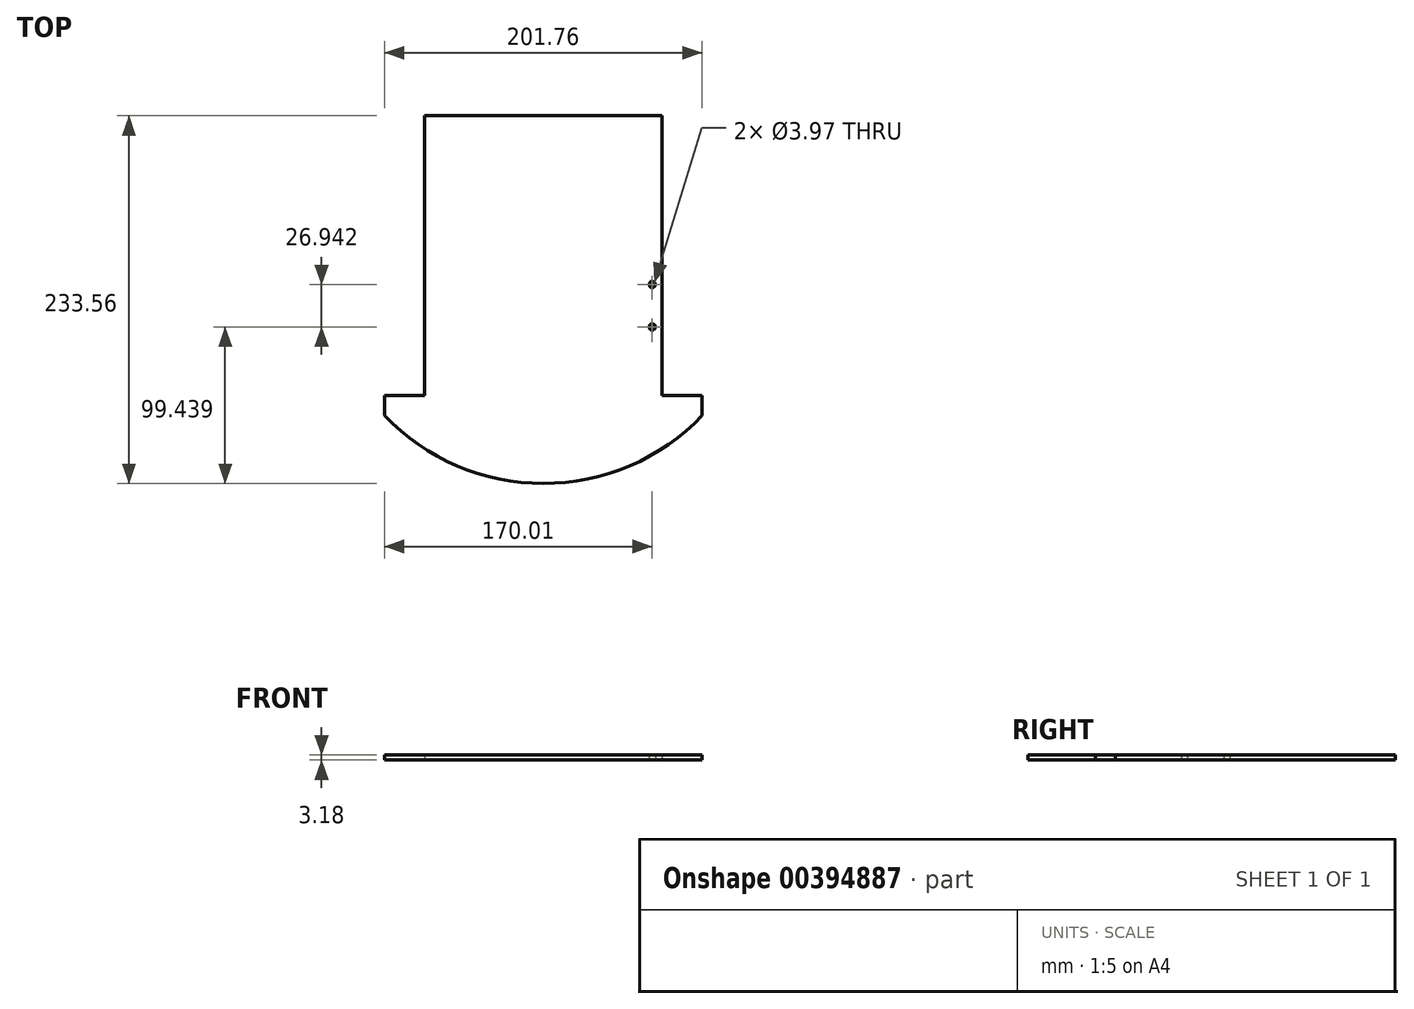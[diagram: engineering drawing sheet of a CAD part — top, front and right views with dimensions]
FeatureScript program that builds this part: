
annotation { "Feature Type Name" : "Feature", "Feature Type Description" : "" }
export const myFeature = defineFeature(function(context is Context, id is Id, definition is map)
    precondition{}
    {
        {
            var Q0;
            Q0=qCreatedBy(makeId("Top.planeOp"),FACE);
            var sketch = newSketch(context, id + "F0", { "sketchPlane" : qUnion([Q0])});
            skLineSegment(sketch, "E0.top", {"start": v(-75.48, 88.9) * mm, "end": v(75.48, 88.9) * mm});
            skLineSegment(sketch, "E0.left", {"start": v(-75.48, -88.9) * mm, "end": v(-75.48, 88.9) * mm});
            skLineSegment(sketch, "E0.right", {"start": v(75.48, -88.9) * mm, "end": v(75.48, 88.9) * mm});
            skPoint(sketch, "E0.middle", {"position": v(0, 0) * mm});
            skLineSegment(sketch, "E1.bottom", {"start": v(-100.88, -88.9) * mm, "end": v(-75.48, -88.9) * mm});
            skLineSegment(sketch, "E1.left", {"start": v(-100.88, -88.9) * mm, "end": v(-100.88, -101.6) * mm});
            skLineSegment(sketch, "E1.right", {"start": v(100.88, -88.9) * mm, "end": v(100.88, -101.6) * mm});
            skPoint(sketch, "E1.middle", {"position": v(0, -95.25) * mm});
            skLineSegment(sketch, "E2.trimOffspring", {"start": v(75.48, -88.9) * mm, "end": v(100.88, -88.9) * mm});
            skArc(sketch, "E3", {"start": v(-100.88, -101.6) * mm, "mid": v(0, -144.66) * mm, "end": v(100.88, -101.6) * mm});
            skSolve(sketch);
        }
        {
            var Q0;
            Q0=makeQuery(id+"F0.imprint","IMPRINT",FACE,{"disambiguationData":[TD([[makeQuery(id+"F0.imprint","IMPRINT",EDGE,{"derivedFrom":sQuery(id+"F0.wireOp",EDGE,"E0.top")}),-1.0]])]});
            extrude(context, id + "F1", {"entities" : qUnion([Q0]), "depth" : 3.17 * mm, "offsetDistance" : 25.4 * mm});
        }
        {
            var Q0;
            Q0=qCreatedBy(makeId("Top.planeOp"),FACE);
            var sketch = newSketch(context, id + "F2", { "sketchPlane" : qUnion([Q0])});
            skLineSegment(sketch, "E4", {"start": v(75.48, -88.9) * mm, "end": v(-75.48, -88.9) * mm, "construction": true});
            skLineSegment(sketch, "E5", {"start": v(69.13, -88.9) * mm, "end": v(69.13, 88.9) * mm, "construction": true});
            skCircle(sketch, "E6", {"center": v(69.13, -45.22) * mm, "radius": 1.98 * mm});
            skCircle(sketch, "E7", {"center": v(69.13, -18.28) * mm, "radius": 1.98 * mm});
            skPoint(sketch, "E8", {"position": v(69.13, -31.75) * mm});
            skLineSegment(sketch, "E9", {"start": v(69.13, -45.22) * mm, "end": v(69.13, -31.75) * mm, "construction": true});
            skLineSegment(sketch, "E10", {"start": v(69.13, -31.75) * mm, "end": v(69.13, -18.28) * mm, "construction": true});
            skCircle(sketch, "E11.MirrorC", {"center": v(-69.13, -18.28) * mm, "radius": 1.98 * mm});
            skCircle(sketch, "E12.MirrorC", {"center": v(-69.13, -45.22) * mm, "radius": 1.98 * mm});
            skSolve(sketch);
        }
        {
            var Q0;
            Q0=makeQuery(id+"F2.imprint","IMPRINT",FACE,{"disambiguationData":[TD([[makeQuery(id+"F2.imprint","IMPRINT",EDGE,{"derivedFrom":sQuery(id+"F2.wireOp",EDGE,"E6")}),1.0]])]});
            var Q1;
            Q1=makeQuery(id+"F2.imprint","IMPRINT",FACE,{"disambiguationData":[TD([[makeQuery(id+"F2.imprint","IMPRINT",EDGE,{"derivedFrom":sQuery(id+"F2.wireOp",EDGE,"E7")}),1.0]])]});
            var Q2;
            Q2=makeQuery(id+"F2.imprint","IMPRINT",FACE,{"disambiguationData":[TD([[makeQuery(id+"F2.imprint","IMPRINT",EDGE,{"derivedFrom":sQuery(id+"F2.wireOp",EDGE,"E12.MirrorC")}),-1.0]])]});
            var Q3;
            Q3=makeQuery(id+"F2.imprint","IMPRINT",FACE,{"disambiguationData":[TD([[makeQuery(id+"F2.imprint","IMPRINT",EDGE,{"derivedFrom":sQuery(id+"F2.wireOp",EDGE,"E11.MirrorC")}),-1.0]])]});
            var Q4;
            Q4=makeQuery(id+"F1.opExtrude","CAP_FACE",FACE,{"disambiguationData":[OSD([sQuery(id+"F0.wireOp",EDGE,"E0.top"),sQuery(id+"F0.wireOp",EDGE,"E0.left"),sQuery(id+"F0.wireOp",EDGE,"E0.right"),sQuery(id+"F0.wireOp",EDGE,"E1.bottom"),sQuery(id+"F0.wireOp",EDGE,"E1.left"),sQuery(id+"F0.wireOp",EDGE,"E1.right"),sQuery(id+"F0.wireOp",EDGE,"E2.trimOffspring"),sQuery(id+"F0.wireOp",EDGE,"E3")])],"isStart":false});
            extrude(context, id + "F3", {"entities" : qUnion([Q0, Q1, Q2, Q3]), "operationType" : NewBodyOperationType.REMOVE, "endBound" : BoundingType.THROUGH_ALL, "depth" : 25.4 * mm, "endBoundEntityFace" : qUnion([Q4]), "offsetDistance" : 25.4 * mm});
        }
    });
